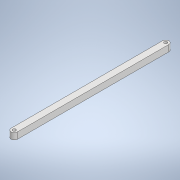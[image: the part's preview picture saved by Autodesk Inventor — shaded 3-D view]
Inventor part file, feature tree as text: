
AUTODESK INVENTOR PART (.ipt)
format: ipt  version: 2020 (Build 240168000, 168)  size: 101,376 bytes
history: native  units: mm
features: extrude x1, sketch x1
ambient origin geometry x8: Origin, YZ Plane, XZ Plane, XY Plane, X Axis, Y Axis, Z Axis, Center Point
bodies: Solid1 (feature_tree)
feature tree (2):
  extrude  "Extrusion1"  Depth=1.0mm
  sketch  "Sketch1"  dims[d0=2.0mm d1=1.0mm d2=47.7mm d3=2.0mm d4=0.0mm]
